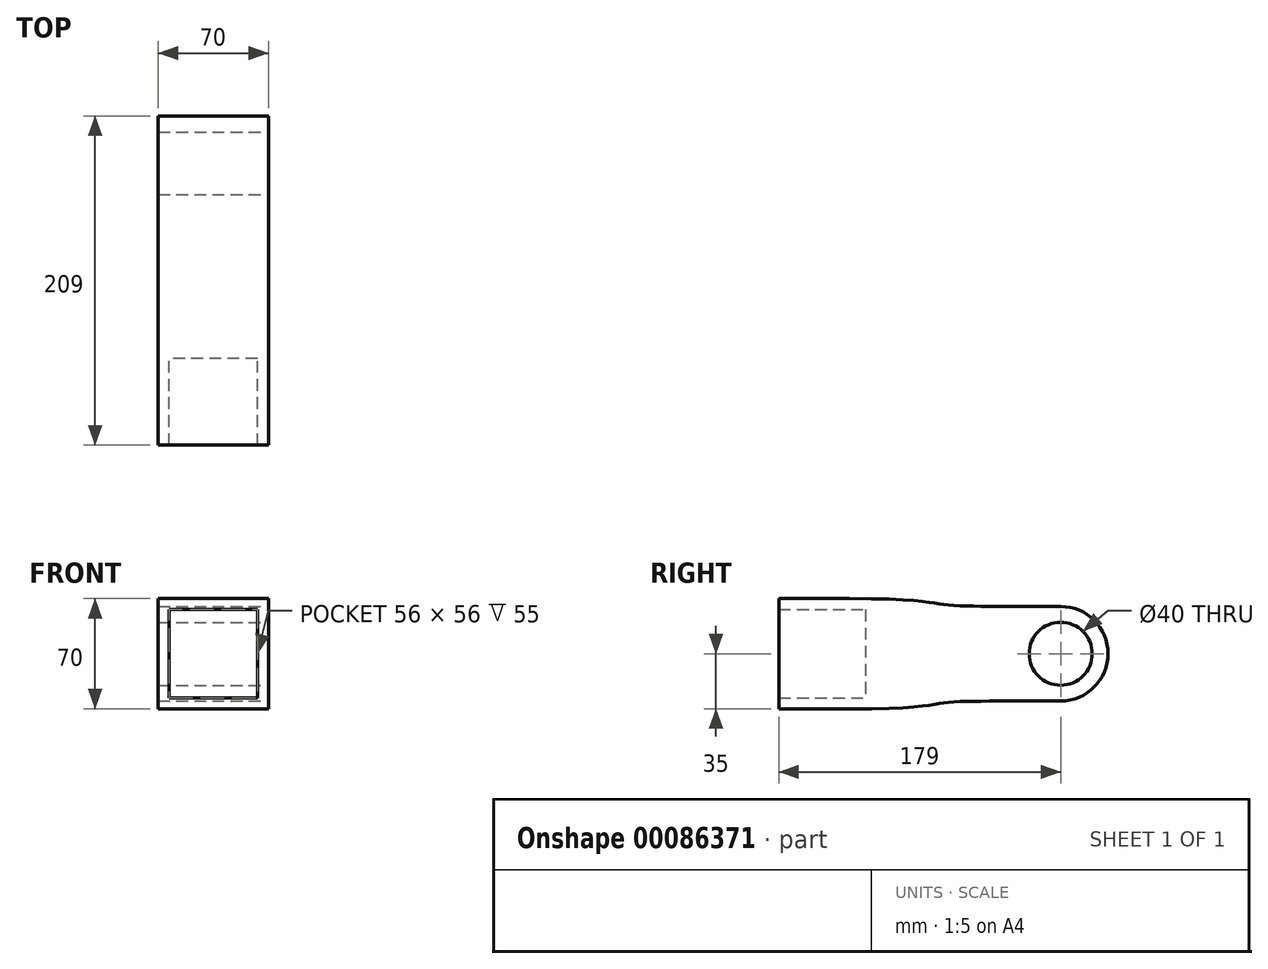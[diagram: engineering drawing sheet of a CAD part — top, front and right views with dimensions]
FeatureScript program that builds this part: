
annotation { "Feature Type Name" : "Feature", "Feature Type Description" : "" }
export const myFeature = defineFeature(function(context is Context, id is Id, definition is map)
    precondition{}
    {
        {
            var Q0;
            Q0=qCreatedBy(makeId("Front.planeOp"),FACE);
            var sketch = newSketch(context, id + "F0", { "sketchPlane" : qUnion([Q0])});
            skLineSegment(sketch, "E0.bottom", {"start": v(28, 28) * mm, "end": v(-28, 28) * mm});
            skLineSegment(sketch, "E0.top", {"start": v(28, -28) * mm, "end": v(-28, -28) * mm});
            skLineSegment(sketch, "E0.left", {"start": v(28, 28) * mm, "end": v(28, -28) * mm});
            skLineSegment(sketch, "E0.right", {"start": v(-28, 28) * mm, "end": v(-28, -28) * mm});
            skPoint(sketch, "E0.middle", {"position": v(0, 0) * mm});
            skLineSegment(sketch, "E1.bottom", {"start": v(35, 35) * mm, "end": v(-35, 35) * mm});
            skLineSegment(sketch, "E1.top", {"start": v(35, -35) * mm, "end": v(-35, -35) * mm});
            skLineSegment(sketch, "E1.left", {"start": v(35, 35) * mm, "end": v(35, -35) * mm});
            skLineSegment(sketch, "E1.right", {"start": v(-35, 35) * mm, "end": v(-35, -35) * mm});
            skSolve(sketch);
        }
        {
            var Q0;
            Q0 = qSketchRegion(id + "F0", true);
            extrude(context, id + "F1", {"entities" : qUnion([Q0]), "depth" : 55 * mm, "offsetDistance" : 25 * mm});
        }
        {
            var Q0;
            Q0=makeQuery(id+"F0.imprint","IMPRINT",FACE,{"disambiguationData":[TD([[makeQuery(id+"F0.imprint","IMPRINT",EDGE,{"derivedFrom":sQuery(id+"F0.wireOp",EDGE,"E0.bottom")}),1.0]])]});
            var Q1;
            Q1=makeQuery(id+"F0.imprint","IMPRINT",FACE,{"disambiguationData":[TD([[makeQuery(id+"F0.imprint","IMPRINT",EDGE,{"derivedFrom":sQuery(id+"F0.wireOp",EDGE,"E0.bottom")}),-1.0]])]});
            var Q2;
            Q2=sQuery(id+"F0.wireOp",EDGE,"E1.bottom");
            var Q3;
            Q3=sQuery(id+"F0.wireOp",EDGE,"E1.left");
            var Q4;
            Q4=sQuery(id+"F0.wireOp",EDGE,"E1.top");
            var Q5;
            Q5=sQuery(id+"F0.wireOp",EDGE,"E1.right");
            extrude(context, id + "F2", {"entities" : qUnion([Q0, Q1]), "operationType" : NewBodyOperationType.ADD, "surfaceEntities" : qUnion([Q2, Q3, Q4, Q5]), "oppositeDirection" : true, "depth" : 380 * mm, "offsetDistance" : 25 * mm});
        }
        {
            var Q0;
            {var subQ0=sQuery(id+"F0.wireOp",EDGE,"E1.left");Q0=makeQuery(id+"F2.boolean.opBoolean","MERGE",FACE,{"derivedFrom":[makeQuery(id+"F1.opExtrude","SWEPT_FACE",FACE,{"disambiguationData":[OSD([subQ0])]}),makeQuery(id+"F2.opExtrude","SWEPT_FACE",FACE,{"disambiguationData":[OSD([subQ0])]})]});}
            var sketch = newSketch(context, id + "F3", { "sketchPlane" : qUnion([Q0])});
            skCircle(sketch, "E2", {"center": v(124, 0) * mm, "radius": 20 * mm});
            skPoint(sketch, "E2.centerSnap0", {"position": v(380, 0) * mm});
            skCircle(sketch, "E3", {"center": v(124, 0) * mm, "radius": 30 * mm});
            skFitSpline(sketch, "E4", {"points": [v(124, 30) * mm, v(70.56, 30.17) * mm, v(50.06, 31.16) * mm, v(-10, 35) * mm], "startDerivative": vector(-166.5, 0) * mm, "endDerivative": vector(-349.43, 0) * mm});
            skLineSegment(sketch, "E5", {"start": v(-55, 0) * mm, "end": v(124, 0) * mm, "construction": true});
            skFitSpline(sketch, "E6.MirrorCS", {"points": [v(124, -30) * mm, v(70.56, -30.17) * mm, v(50.06, -31.16) * mm, v(-10, -35) * mm], "startDerivative": vector(-166.5, 0) * mm, "endDerivative": vector(-349.43, 0) * mm});
            skSolve(sketch);
        }
        {
            var Q0;
            {var subQ3=sQuery(id+"F3.wireOp",EDGE,"E4");Q0=makeQuery(id+"F3.imprint","IMPRINT",FACE,{"disambiguationData":[TD([[makeQuery(id+"F3.imprint","IMPRINT",EDGE,{"derivedFrom":subQ3}),-1.0]])]});}
            var Q1;
            Q1=makeQuery(id+"F3.imprint","IMPRINT",FACE,{"disambiguationData":[TD([[makeQuery(id+"F3.imprint","IMPRINT",EDGE,{"derivedFrom":sQuery(id+"F3.wireOp",EDGE,"E2")}),1.0]])]});
            extrude(context, id + "F4", {"entities" : qUnion([Q0, Q1]), "operationType" : NewBodyOperationType.REMOVE, "endBound" : BoundingType.THROUGH_ALL, "oppositeDirection" : true, "depth" : 25 * mm, "offsetDistance" : 25 * mm});
        }
    });
